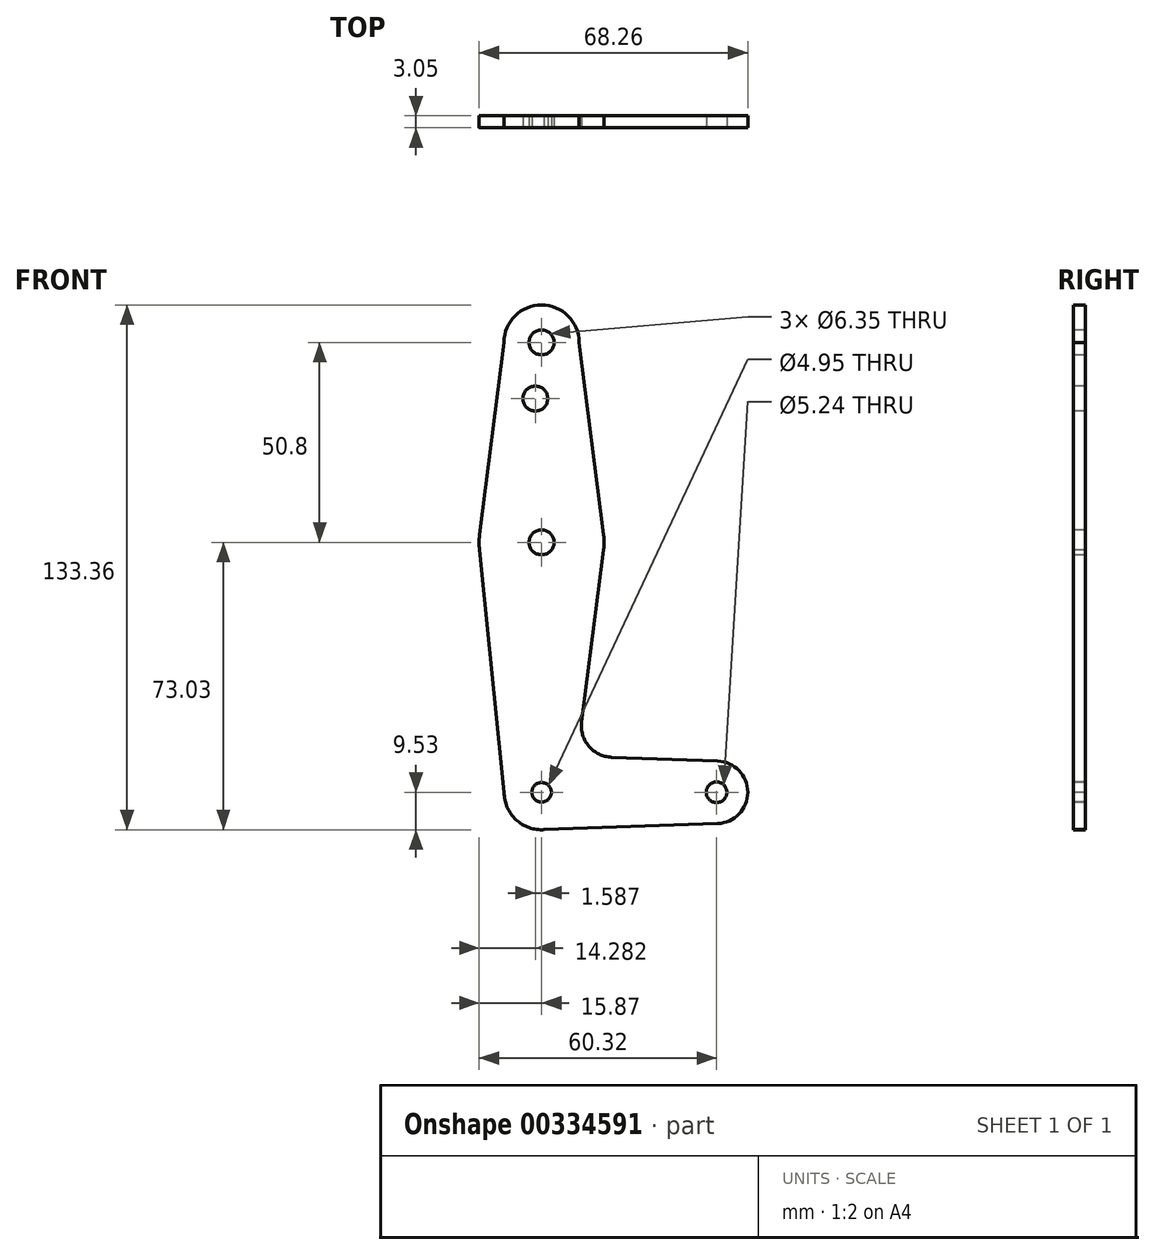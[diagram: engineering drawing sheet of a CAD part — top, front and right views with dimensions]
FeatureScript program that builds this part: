
annotation { "Feature Type Name" : "Feature", "Feature Type Description" : "" }
export const myFeature = defineFeature(function(context is Context, id is Id, definition is map)
    precondition{}
    {
        {
            var Q0;
            Q0=qCreatedBy(makeId("Front.planeOp"),FACE);
            var sketch = newSketch(context, id + "F0", { "sketchPlane" : qUnion([Q0])});
            skCircle(sketch, "E0", {"center": v(0, 0) * mm, "radius": 9.53 * mm});
            skLineSegment(sketch, "E1", {"start": v(0, 0) * mm, "end": v(0, 63.5) * mm, "construction": true});
            skCircle(sketch, "E2", {"center": v(0, 63.5) * mm, "radius": 15.88 * mm});
            skLineSegment(sketch, "E3", {"start": v(0, 63.5) * mm, "end": v(0, 114.3) * mm, "construction": true});
            skCircle(sketch, "E4", {"center": v(0, 114.3) * mm, "radius": 9.52 * mm});
            skLineSegment(sketch, "E5", {"start": v(0, 0) * mm, "end": v(44.45, 0) * mm, "construction": true});
            skCircle(sketch, "E6", {"center": v(44.45, 0) * mm, "radius": 7.94 * mm});
            skLineSegment(sketch, "E7", {"start": v(0, -9.53) * mm, "end": v(44.73, -7.93) * mm});
            skLineSegment(sketch, "E8", {"start": v(17.78, 8.9) * mm, "end": v(44.73, 7.93) * mm});
            skLineSegment(sketch, "E9", {"start": v(-9.52, 114.3) * mm, "end": v(-15.75, 65.5) * mm});
            skLineSegment(sketch, "E10", {"start": v(-9.53, 0) * mm, "end": v(-15.75, 61.5) * mm});
            skLineSegment(sketch, "E11", {"start": v(9.52, 114.3) * mm, "end": v(16, 63.5) * mm});
            skLineSegment(sketch, "E12", {"start": v(15.75, 61.5) * mm, "end": v(10.18, 17.84) * mm});
            skCircle(sketch, "E13", {"center": v(0, 114.3) * mm, "radius": 3.18 * mm});
            skCircle(sketch, "E14", {"center": v(-1.59, 100.03) * mm, "radius": 3.18 * mm});
            skCircle(sketch, "E15", {"center": v(0, 63.5) * mm, "radius": 3.18 * mm});
            skCircle(sketch, "E16", {"center": v(0, 0) * mm, "radius": 2.48 * mm});
            skCircle(sketch, "E17", {"center": v(44.45, 0) * mm, "radius": 2.62 * mm});
            skArc(sketch, "E18.filletArc", {"start": v(10.18, 17.84) * mm, "mid": v(12, 11.69) * mm, "end": v(17.78, 8.9) * mm});
            skSolve(sketch);
        }
        {
            var Q0;
            Q0 = qSketchRegion(id + "F0", true);
            extrude(context, id + "F1", {"entities" : qUnion([Q0]), "oppositeDirection" : true, "depth" : 3.05 * mm});
        }
    });
